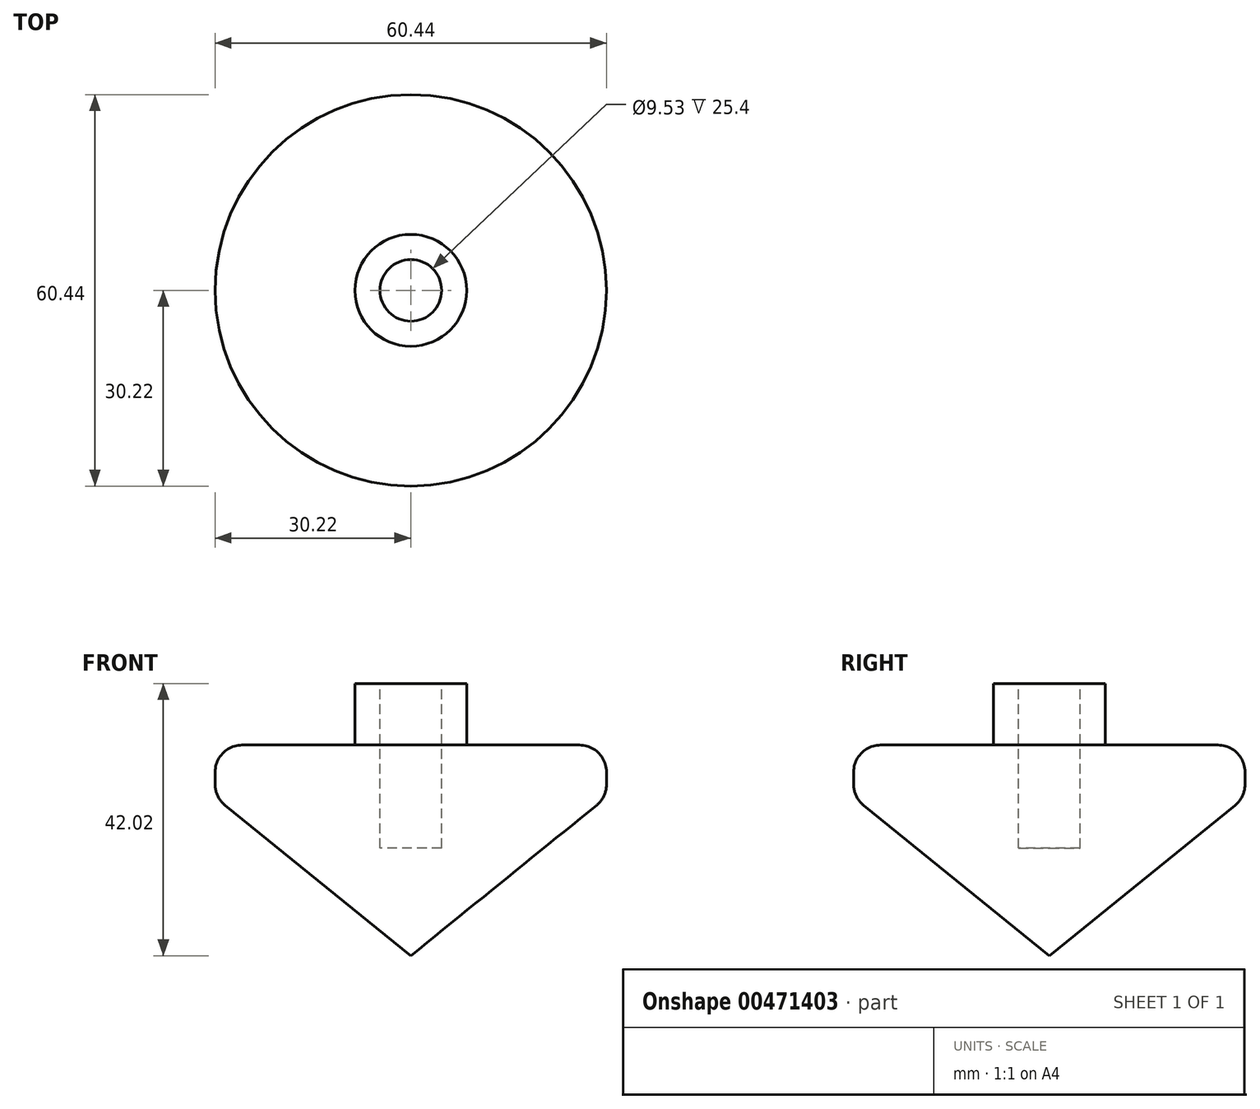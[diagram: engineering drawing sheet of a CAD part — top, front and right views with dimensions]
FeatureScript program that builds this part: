
annotation { "Feature Type Name" : "Feature", "Feature Type Description" : "" }
export const myFeature = defineFeature(function(context is Context, id is Id, definition is map)
    precondition{}
    {
        {
            var Q0;
            Q0=qCreatedBy(makeId("Front.planeOp"),FACE);
            var sketch = newSketch(context, id + "F0", { "sketchPlane" : qUnion([Q0])});
            skLineSegment(sketch, "E0", {"start": v(0, 0) * mm, "end": v(28.68, 23.22) * mm});
            skLineSegment(sketch, "E1", {"start": v(30.22, 26.44) * mm, "end": v(30.22, 28.37) * mm});
            skLineSegment(sketch, "E2", {"start": v(26.07, 32.52) * mm, "end": v(8.63, 32.52) * mm});
            skLineSegment(sketch, "E3", {"start": v(8.63, 32.52) * mm, "end": v(8.63, 42.02) * mm});
            skLineSegment(sketch, "E4", {"start": v(8.63, 42.02) * mm, "end": v(0, 42.02) * mm});
            skLineSegment(sketch, "E5", {"start": v(0, 42.02) * mm, "end": v(0, 0) * mm});
            skPoint(sketch, "E6.visualSharp", {"position": v(30.22, 32.52) * mm});
            skArc(sketch, "E6.filletArc", {"start": v(30.22, 28.37) * mm, "mid": v(29, 31.3) * mm, "end": v(26.07, 32.52) * mm});
            skPoint(sketch, "E7.visualSharp", {"position": v(30.22, 24.46) * mm});
            skArc(sketch, "E7.filletArc", {"start": v(28.68, 23.22) * mm, "mid": v(29.82, 24.66) * mm, "end": v(30.22, 26.44) * mm});
            skSolve(sketch);
        }
        {
            var Q0;
            Q0 = qSketchRegion(id + "F0", true);
            var Q1;
            Q1=sQuery(id+"F0.wireOp",EDGE,"E5");
            revolve(context, id + "F1", {"entities" : qUnion([Q0]), "axis" : qUnion([Q1]), "revolveType" : RevolveType.FULL});
        }
        {
            var Q0;
            Q0=makeQuery(id+"F1.opRevolve","SWEPT_FACE",FACE,{"disambiguationData":[OSD([sQuery(id+"F0.wireOp",EDGE,"E4")])]});
            var sketch = newSketch(context, id + "F2", { "sketchPlane" : qUnion([Q0])});
            skCircle(sketch, "E8", {"center": v(0, 0) * mm, "radius": 4.76 * mm});
            skSolve(sketch);
        }
        {
            var Q0;
            Q0 = qSketchRegion(id + "F2", true);
            extrude(context, id + "F3", {"entities" : qUnion([Q0]), "operationType" : NewBodyOperationType.REMOVE, "oppositeDirection" : true, "depth" : 25.4 * mm});
        }
    });
